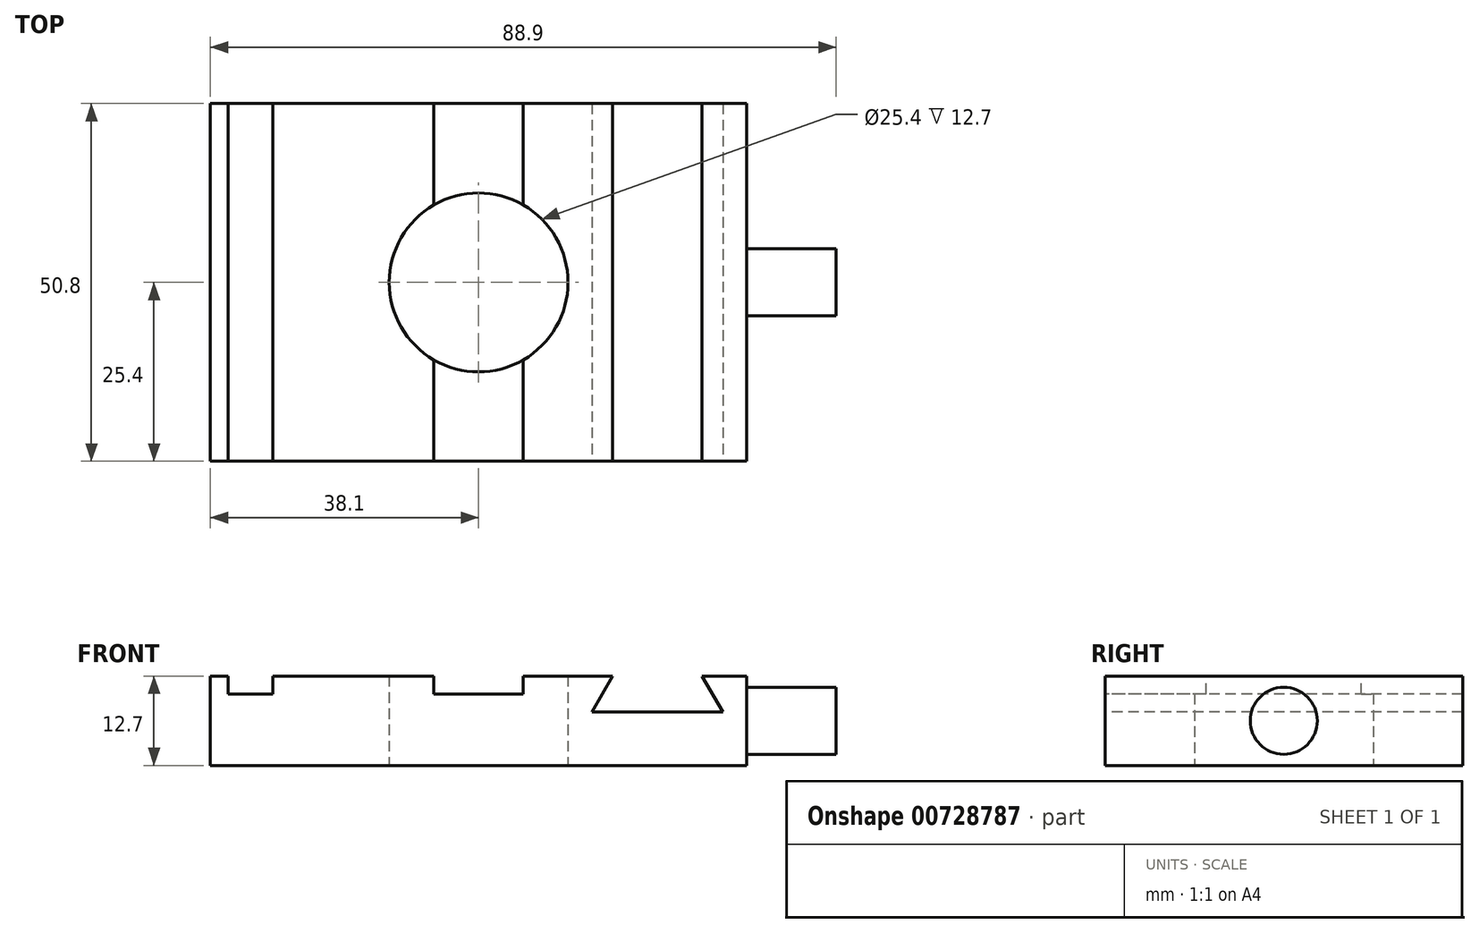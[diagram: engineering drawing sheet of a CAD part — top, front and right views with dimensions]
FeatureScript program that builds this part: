
annotation { "Feature Type Name" : "Feature", "Feature Type Description" : "" }
export const myFeature = defineFeature(function(context is Context, id is Id, definition is map)
    precondition{}
    {
        {
            var Q0;
            Q0=qCreatedBy(makeId("Top.planeOp"),FACE);
            var sketch = newSketch(context, id + "F0", { "sketchPlane" : qUnion([Q0])});
            skLineSegment(sketch, "E0.bottom", {"start": v(38.1, 25.4) * mm, "end": v(-38.1, 25.4) * mm});
            skLineSegment(sketch, "E0.top", {"start": v(38.1, -25.4) * mm, "end": v(-38.1, -25.4) * mm});
            skLineSegment(sketch, "E0.left", {"start": v(38.1, 25.4) * mm, "end": v(38.1, -25.4) * mm});
            skLineSegment(sketch, "E0.right", {"start": v(-38.1, 25.4) * mm, "end": v(-38.1, -25.4) * mm});
            skPoint(sketch, "E0.middle", {"position": v(0, 0) * mm});
            skCircle(sketch, "E1", {"center": v(0, 0) * mm, "radius": 12.7 * mm});
            skSolve(sketch);
        }
        {
            var Q0;
            Q0=makeQuery(id+"F0.imprint","IMPRINT",FACE,{"disambiguationData":[TD([[makeQuery(id+"F0.imprint","IMPRINT",EDGE,{"derivedFrom":sQuery(id+"F0.wireOp",EDGE,"E0.bottom")}),1.0]])]});
            extrude(context, id + "F1", {"entities" : qUnion([Q0]), "depth" : 12.7 * mm, "offsetDistance" : 25.4 * mm});
        }
        {
            var Q0;
            Q0=makeQuery(id+"F1.opExtrude","CAP_FACE",FACE,{"disambiguationData":[OSD([sQuery(id+"F0.wireOp",EDGE,"E0.bottom"),sQuery(id+"F0.wireOp",EDGE,"E0.top"),sQuery(id+"F0.wireOp",EDGE,"E0.left"),sQuery(id+"F0.wireOp",EDGE,"E0.right"),sQuery(id+"F0.wireOp",EDGE,"E1")])],"isStart":false});
            var sketch = newSketch(context, id + "F2", { "sketchPlane" : qUnion([Q0])});
            skLineSegment(sketch, "E2.bottom", {"start": v(-35.56, 25.4) * mm, "end": v(-29.21, 25.4) * mm});
            skLineSegment(sketch, "E2.top", {"start": v(-35.56, -25.4) * mm, "end": v(-29.21, -25.4) * mm});
            skLineSegment(sketch, "E2.left", {"start": v(-35.56, 25.4) * mm, "end": v(-35.56, -25.4) * mm});
            skLineSegment(sketch, "E2.right", {"start": v(-29.21, 25.4) * mm, "end": v(-29.21, -25.4) * mm});
            skLineSegment(sketch, "E3", {"start": v(-6.35, 25.4) * mm, "end": v(-6.35, -25.4) * mm});
            skLineSegment(sketch, "E4", {"start": v(-6.35, -25.4) * mm, "end": v(6.35, -25.4) * mm});
            skLineSegment(sketch, "E5", {"start": v(6.35, -25.4) * mm, "end": v(6.35, 25.4) * mm});
            skLineSegment(sketch, "E6", {"start": v(6.35, 25.4) * mm, "end": v(-6.35, 25.4) * mm});
            skLineSegment(sketch, "E7", {"start": v(0, 25.4) * mm, "end": v(0, -25.4) * mm, "construction": true});
            skPoint(sketch, "E8", {"position": v(0, 0) * mm});
            skSolve(sketch);
        }
        {
            var Q0;
            {var subQ0=sQuery(id+"F2.wireOp",EDGE,"E6");Q0=makeQuery(id+"F2.imprint","IMPRINT",FACE,{"disambiguationData":[TD([[makeQuery(id+"F2.imprint","IMPRINT",EDGE,{"derivedFrom":subQ0}),1.0]])]});}
            var Q1;
            {var subQ0=sQuery(id+"F2.wireOp",EDGE,"E4");Q1=makeQuery(id+"F2.imprint","IMPRINT",FACE,{"disambiguationData":[TD([[makeQuery(id+"F2.imprint","IMPRINT",EDGE,{"derivedFrom":subQ0}),-1.0]])]});}
            var Q2;
            Q2=makeQuery(id+"F2.imprint","IMPRINT",FACE,{"disambiguationData":[TD([[makeQuery(id+"F2.imprint","IMPRINT",EDGE,{"derivedFrom":sQuery(id+"F2.wireOp",EDGE,"E2.bottom")}),1.0]])]});
            extrude(context, id + "F3", {"entities" : qUnion([Q0, Q1, Q2]), "operationType" : NewBodyOperationType.REMOVE, "oppositeDirection" : true, "depth" : 2.54 * mm, "offsetDistance" : 25.4 * mm});
        }
        {
            var Q0;
            Q0=makeQuery(id+"F1.opExtrude","SWEPT_FACE",FACE,{"disambiguationData":[OSD([sQuery(id+"F0.wireOp",EDGE,"E0.top")])]});
            var sketch = newSketch(context, id + "F4", { "sketchPlane" : qUnion([Q0])});
            skLineSegment(sketch, "E9", {"start": v(19.05, 12.7) * mm, "end": v(16.12, 7.62) * mm});
            skLineSegment(sketch, "E10", {"start": v(16.12, 7.62) * mm, "end": v(34.68, 7.62) * mm});
            skLineSegment(sketch, "E11", {"start": v(34.68, 7.62) * mm, "end": v(31.75, 12.7) * mm});
            skLineSegment(sketch, "E12", {"start": v(31.75, 12.7) * mm, "end": v(19.05, 12.7) * mm});
            skLineSegment(sketch, "E13", {"start": v(25.4, 12.7) * mm, "end": v(25.4, 7.62) * mm, "construction": true});
            skSolve(sketch);
        }
        {
            var Q0;
            Q0=makeQuery(id+"F4.imprint","IMPRINT",FACE,{"disambiguationData":[TD([[makeQuery(id+"F4.imprint","IMPRINT",EDGE,{"derivedFrom":sQuery(id+"F4.wireOp",EDGE,"E9")}),1.0]])]});
            extrude(context, id + "F5", {"entities" : qUnion([Q0]), "operationType" : NewBodyOperationType.REMOVE, "endBound" : BoundingType.THROUGH_ALL, "oppositeDirection" : true, "depth" : 25.4 * mm, "offsetDistance" : 25.4 * mm});
        }
        {
            var Q0;
            Q0=makeQuery(id+"F1.opExtrude","SWEPT_FACE",FACE,{"disambiguationData":[OSD([sQuery(id+"F0.wireOp",EDGE,"E0.left")])]});
            var sketch = newSketch(context, id + "F6", { "sketchPlane" : qUnion([Q0])});
            skCircle(sketch, "E14", {"center": v(0, 6.35) * mm, "radius": 4.76 * mm});
            skPoint(sketch, "E14.centerSnap0", {"position": v(-25.4, 6.35) * mm});
            skPoint(sketch, "E14.centerSnap1", {"position": v(0, 12.7) * mm});
            skSolve(sketch);
        }
        {
            var Q0;
            Q0=makeQuery(id+"F6.imprint","IMPRINT",FACE,{"disambiguationData":[TD([[makeQuery(id+"F6.imprint","IMPRINT",EDGE,{"derivedFrom":sQuery(id+"F6.wireOp",EDGE,"E14")}),1.0]])]});
            extrude(context, id + "F7", {"entities" : qUnion([Q0]), "operationType" : NewBodyOperationType.ADD, "depth" : 12.7 * mm, "offsetDistance" : 25.4 * mm});
        }
    });
